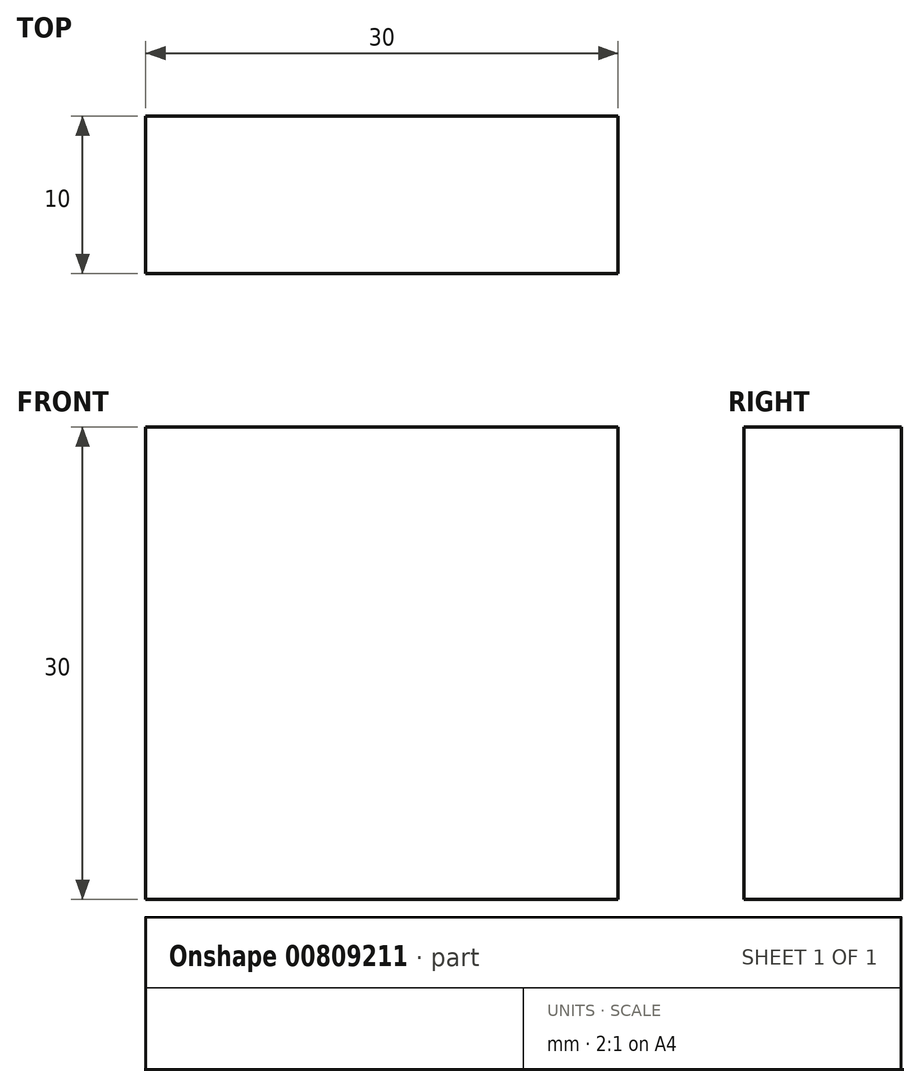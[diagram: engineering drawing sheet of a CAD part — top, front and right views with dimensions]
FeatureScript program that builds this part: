
annotation { "Feature Type Name" : "Feature", "Feature Type Description" : "" }
export const myFeature = defineFeature(function(context is Context, id is Id, definition is map)
    precondition{}
    {
        {
            var Q0;
            Q0=qCreatedBy(makeId("Top.planeOp"),FACE);
            var sketch = newSketch(context, id + "F0", { "sketchPlane" : qUnion([Q0])});
            skLineSegment(sketch, "E0.bottom", {"start": v(30, 10) * mm, "end": v(0, 10) * mm});
            skLineSegment(sketch, "E0.top", {"start": v(30, 0) * mm, "end": v(0, 0) * mm});
            skLineSegment(sketch, "E0.left", {"start": v(30, 10) * mm, "end": v(30, 0) * mm});
            skLineSegment(sketch, "E0.right", {"start": v(0, 10) * mm, "end": v(0, 0) * mm});
            skSolve(sketch);
        }
        {
            var Q0;
            Q0=makeQuery(id+"F0.imprint","IMPRINT",FACE,{"disambiguationData":[TD([[makeQuery(id+"F0.imprint","IMPRINT",EDGE,{"derivedFrom":sQuery(id+"F0.wireOp",EDGE,"E0.bottom")}),1.0]])]});
            extrude(context, id + "F1", {"entities" : qUnion([Q0]), "depth" : 30 * mm, "offsetDistance" : 25.4 * mm});
        }
    });
